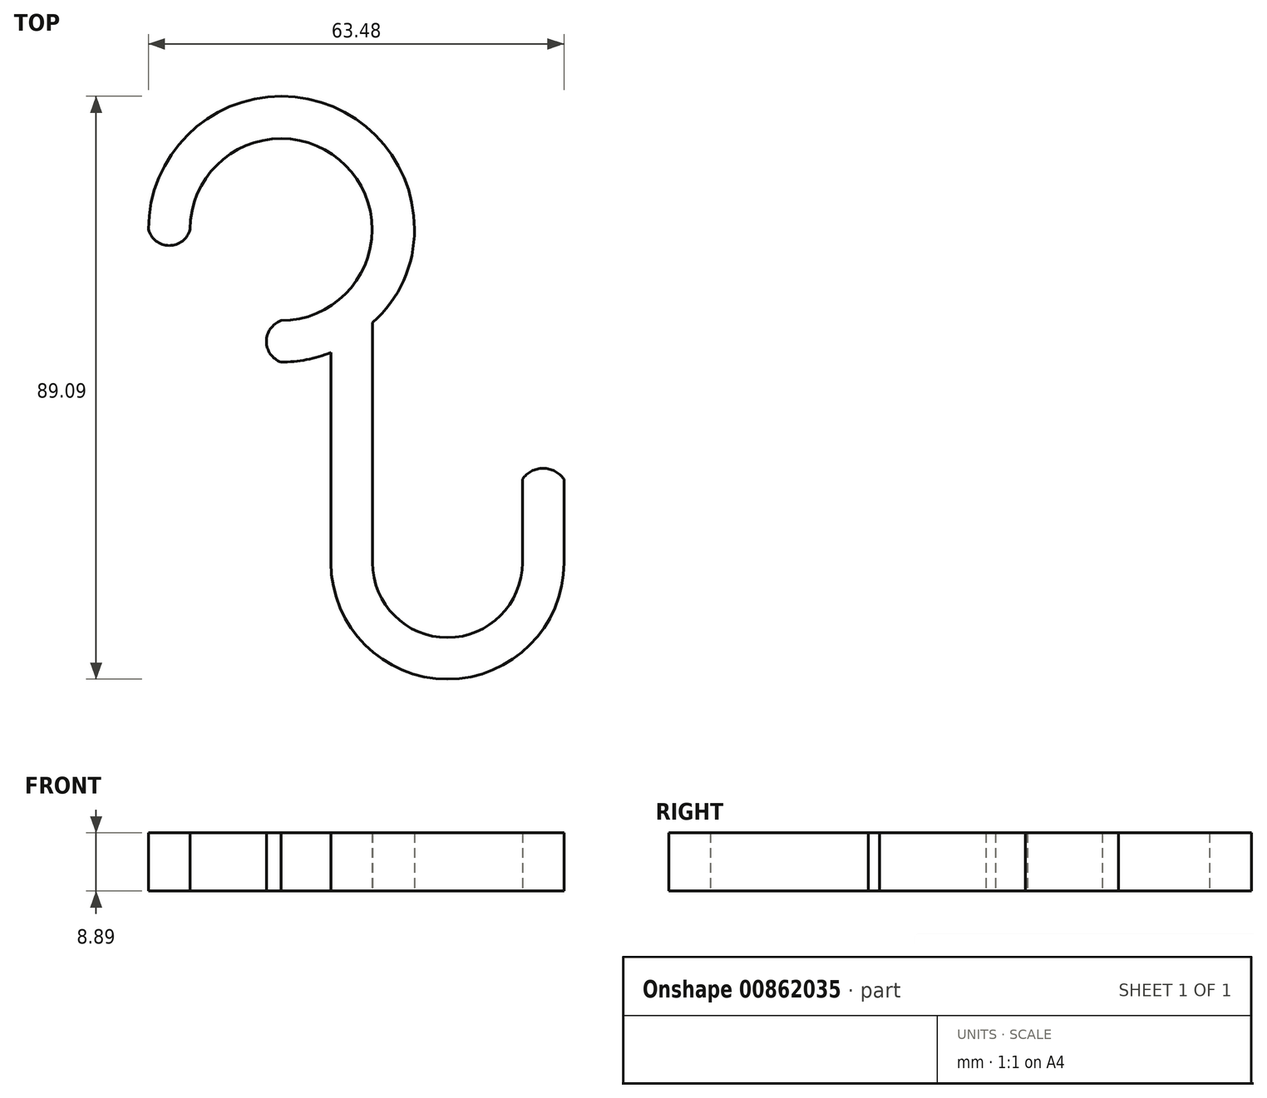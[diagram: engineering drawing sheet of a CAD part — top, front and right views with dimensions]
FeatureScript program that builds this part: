
annotation { "Feature Type Name" : "Feature", "Feature Type Description" : "" }
export const myFeature = defineFeature(function(context is Context, id is Id, definition is map)
    precondition{}
    {
        {
            var Q0;
            Q0=qCreatedBy(makeId("Top.planeOp"),FACE);
            var sketch = newSketch(context, id + "F0", { "sketchPlane" : qUnion([Q0])});
            skLineSegment(sketch, "E0", {"start": v(-23.96, 1.75) * mm, "end": v(-23.96, -30.38) * mm});
            skArc(sketch, "E1", {"start": v(-17.61, -30.38) * mm, "mid": v(-6.16, -41.83) * mm, "end": v(5.29, -30.38) * mm});
            skArc(sketch, "E2.0", {"start": v(-23.96, -30.38) * mm, "mid": v(-6.16, -48.18) * mm, "end": v(11.64, -30.38) * mm});
            skLineSegment(sketch, "E3", {"start": v(5.29, -30.38) * mm, "end": v(5.29, -17.65) * mm});
            skLineSegment(sketch, "E4", {"start": v(11.64, -30.38) * mm, "end": v(11.64, -17.65) * mm});
            skArc(sketch, "E5", {"start": v(11.64, -17.65) * mm, "mid": v(8.46, -15.95) * mm, "end": v(5.29, -17.65) * mm});
            skArc(sketch, "E6.0", {"start": v(-11.2, 20.59) * mm, "mid": v(-31.52, 40.9) * mm, "end": v(-51.84, 20.59) * mm});
            skArc(sketch, "E7.0", {"start": v(-31.58, 0.27) * mm, "mid": v(-27.7, 0.64) * mm, "end": v(-23.96, 1.75) * mm});
            skArc(sketch, "E8", {"start": v(-31.58, 6.62) * mm, "mid": v(-33.82, 3.44) * mm, "end": v(-31.58, 0.27) * mm});
            skArc(sketch, "E9", {"start": v(-17.61, 6.33) * mm, "mid": v(-12.84, 12.75) * mm, "end": v(-11.2, 20.59) * mm});
            skLineSegment(sketch, "E10.trimOffspring", {"start": v(-17.61, 6.33) * mm, "end": v(-17.61, -30.38) * mm});
            skArc(sketch, "E11", {"start": v(-51.84, 20.59) * mm, "mid": v(-48.67, 18.1) * mm, "end": v(-45.5, 20.59) * mm});
            skArc(sketch, "E12", {"start": v(-31.58, 6.62) * mm, "mid": v(-21.72, 30.34) * mm, "end": v(-45.5, 20.59) * mm});
            skPoint(sketch, "E13.trimOffspring.start.orphan", {"position": v(-17.61, 20.53) * mm});
            skSolve(sketch);
        }
        {
            var Q0;
            Q0=makeQuery(id+"F0.imprint","IMPRINT",FACE,{"disambiguationData":[TD([[makeQuery(id+"F0.imprint","IMPRINT",EDGE,{"derivedFrom":sQuery(id+"F0.wireOp",EDGE,"E0")}),1.0]])]});
            extrude(context, id + "F1", {"entities" : qUnion([Q0]), "depth" : 8.9 * mm, "offsetDistance" : 25.4 * mm});
        }
    });
